# Revit family: Casement_34_G_Top_Hung_Standard
name_source: partatom
category: Windows
revit_build: Autodesk Revit 2014 (Build: 20130308_1515(x64)
units: mm (PartAtom-declared; Revit-internal decimal feet)

## types (12) — shared parameters
Aluminium Thickness = 1 mm  [stored 0.00328084 ft]
Bead SG Gap = 13 mm  [stored 0.0426509 ft]
Bottom Hung = No
Casement Dimension = 34 mm  [stored 0.111549 ft]
Custom Sash Height Bottom = 569 mm  [stored 1.8668 ft]
Custom Sash Height Top = 569 mm  [stored 1.8668 ft]
Custom Window Height = 1190 mm  [stored 3.9042 ft]
DG Extrusion Start = 7 mm  [stored 0.0229659 ft]
DG Gasket Finish = Double Glazing Gasket Material
DG Thickness Calc = 4 mm  [stored 0.0131234 ft]
Default Sill Height = 800 mm  [stored 2.62467 ft]
Depth Bead = 20 mm  [stored 0.0656168 ft]
Description = Window 34mm, Type G top hung
Frame Center Offset = 17 mm  [stored 0.0557743 ft]
Height = 1200 mm  [stored 3.93701 ft]
Height Panel 1 = 555 mm  [stored 1.82087 ft]
Height Panel 2 = 555 mm  [stored 1.82087 ft]
Height Panel 4 = 1140 mm  [stored 3.74016 ft]
Height Sash 1 = 539 mm
Height Sash 2 = 539 mm
Height Sash Bottom Opening = 569 mm  [stored 1.8668 ft]
Height Sash Top Opening = 569 mm  [stored 1.8668 ft]
Length Mullion = 1200 mm  [stored 3.93701 ft]
Limit Fixed Pane Height Max = 1800 mm
Limit Fixed Pane Height Min = 200 mm  [stored 0.656168 ft]
Limit Fixed Pane Width Max = 1500 mm
Limit Fixed Pane Width Min = 200 mm  [stored 0.656168 ft]
Limit Sash Bottom Height Max Based On Top Sash = 1229 mm
Limit Sash Height Bottom Max = 900 mm  [stored 2.95276 ft]
Limit Sash Height Bottom Min = 300 mm  [stored 0.984252 ft]
Limit Sash Height Top Max = 900 mm  [stored 2.95276 ft]
Limit Sash Height Top Min = 300 mm  [stored 0.984252 ft]
Limit Sash Width Max = 1200 mm  [stored 3.93701 ft]
Limit Sash Width Min = 300 mm  [stored 0.984252 ft]
Limit Window Height Max = 1860 mm
Manufacturer = Crealco
Max System DG One Piece Thickness = 4 mm  [stored 0.0131234 ft]
Max System DG Unit Thickness = 20 mm  [stored 0.0656168 ft]
Model = Casement 34
Offset Bead SG Center Reversed = 17 mm  [stored 0.0557743 ft]
Offset Sash 1 Top = 23 mm  [stored 0.0754593 ft]
Offset Sash 2 Top = 608 mm  [stored 1.99475 ft]
Offset Sash Left = 23 mm  [stored 0.0754593 ft]
Offset Transom 1 Top = 585 mm  [stored 1.91929 ft]
Offset Window Exterior = 17 mm  [stored 0.0557743 ft]
Rough Width = 16 mm  [stored 0.0524934 ft]
SG Gasket Thickness = 6 mm  [stored 0.019685 ft]
Sash Center Offset = 14 mm  [stored 0.0459318 ft]
Sash Overlap = 7 mm  [stored 0.0229659 ft]
Sash Spacing Inner = 8 mm  [stored 0.0262467 ft]
Top Hung = Yes
URL = http://www.crealco.co.za
Wall Closure = By host
Width Bead = 15 mm  [stored 0.0492126 ft]
Width Profile = 30 mm  [stored 0.0984252 ft]
zero-valued in all types: Window Exterior Offset

## per-type parameters (varying)
- 34-1212DT-1000Pa: Area Pane Left Bottom=0.25 m²; Area Pane Left Top=0.25 m²; Area Pane Right=0.6 m²; Clearvue Insulated LowE SHGC Value=0.658; Clearvue Insulated LowE U Value=4.66; Clearvue Insulated SHGC Value=0.723; Clearvue Insulated U Value=5.43; Clearvue SHGC Value=0.814; Clearvue U Value=8.2; Custom Sash Width=569 mm  [stored 1.8668 ft]; Custom Windload=1000 mm  [stored 3.28084 ft]; Custom Window Width=1190 mm  [stored 3.9042 ft]; Depth Mullion=35 mm; Energy Advantage SHGC Value=0.729; Energy Advantage U Value=6.26; Intruderprufe LowE SHGC Value=0.682; Intruderprufe LowE U Value=6.03; Intruderprufe SHGC Value=0.768; Intruderprufe U Value=8.08; Length Transom=555 mm  [stored 1.82087 ft]; Limit Window Width Max=2145 mm; Limit Window Width Min=845 mm  [stored 2.77231 ft]; Max Pane Area=0.6 m²; Mullion Depth Windload Based=35 mm; Offset Mullion Left=585 mm  [stored 1.91929 ft]; Offset Panel 4 Left=615 mm  [stored 2.01772 ft]; Width=1190 mm  [stored 3.9042 ft]; Width Panel 1=555 mm  [stored 1.82087 ft]; Width Panel 2=555 mm  [stored 1.82087 ft]; Width Panel 4=545 mm; Width Sash 1=539 mm; Width Sash 2=539 mm; Width Sash Opening=569 mm  [stored 1.8668 ft]; Windload Design=1000 mm  [stored 3.28084 ft]
- 34-1212DT-1500Pa: Area Pane Left Bottom=0.25 m²; Area Pane Left Top=0.25 m²; Area Pane Right=0.6 m²; Clearvue Insulated LowE SHGC Value=0.659; Clearvue Insulated LowE U Value=4.78; Clearvue Insulated SHGC Value=0.737; Clearvue Insulated U Value=5.35; Clearvue SHGC Value=0.814; Clearvue U Value=8.23; Custom Sash Width=569 mm  [stored 1.8668 ft]; Custom Windload=1500 mm; Custom Window Width=1190 mm  [stored 3.9042 ft]; Depth Mullion=54 mm  [stored 0.177165 ft]; Energy Advantage SHGC Value=0.73; Energy Advantage U Value=6.35; Intruderprufe LowE SHGC Value=0.684; Intruderprufe LowE U Value=6.12; Intruderprufe SHGC Value=0.766; Intruderprufe U Value=7.92; Length Transom=555 mm  [stored 1.82087 ft]; Limit Window Width Max=2145 mm; Limit Window Width Min=845 mm  [stored 2.77231 ft]; Max Pane Area=0.6 m²; Mullion Depth Windload Based=54 mm  [stored 0.177165 ft]; Offset Mullion Left=585 mm  [stored 1.91929 ft]; Offset Panel 4 Left=615 mm  [stored 2.01772 ft]; Width=1190 mm  [stored 3.9042 ft]; Width Panel 1=555 mm  [stored 1.82087 ft]; Width Panel 2=555 mm  [stored 1.82087 ft]; Width Panel 4=545 mm; Width Sash 1=539 mm; Width Sash 2=539 mm; Width Sash Opening=569 mm  [stored 1.8668 ft]; Windload Design=1500 mm
- 34-1212DT-2000Pa: Area Pane Left Bottom=0.25 m²; Area Pane Left Top=0.25 m²; Area Pane Right=0.6 m²; Clearvue Insulated LowE SHGC Value=0.659; Clearvue Insulated LowE U Value=4.78; Clearvue Insulated SHGC Value=0.737; Clearvue Insulated U Value=5.35; Clearvue SHGC Value=0.814; Clearvue U Value=8.23; Custom Sash Width=569 mm  [stored 1.8668 ft]; Custom Windload=2000 mm; Custom Window Width=1190 mm  [stored 3.9042 ft]; Depth Mullion=54 mm  [stored 0.177165 ft]; Energy Advantage SHGC Value=0.73; Energy Advantage U Value=6.35; Intruderprufe LowE SHGC Value=0.684; Intruderprufe LowE U Value=6.12; Intruderprufe SHGC Value=0.766; Intruderprufe U Value=7.92; Length Transom=555 mm  [stored 1.82087 ft]; Limit Window Width Max=2145 mm; Limit Window Width Min=845 mm  [stored 2.77231 ft]; Max Pane Area=0.6 m²; Mullion Depth Windload Based=54 mm  [stored 0.177165 ft]; Offset Mullion Left=585 mm  [stored 1.91929 ft]; Offset Panel 4 Left=615 mm  [stored 2.01772 ft]; Width=1190 mm  [stored 3.9042 ft]; Width Panel 1=555 mm  [stored 1.82087 ft]; Width Panel 2=555 mm  [stored 1.82087 ft]; Width Panel 4=545 mm; Width Sash 1=539 mm; Width Sash 2=539 mm; Width Sash Opening=569 mm  [stored 1.8668 ft]; Windload Design=2000 mm
- 34-1512DT-1000Pa: Area Pane Left Bottom=0.25 m²; Area Pane Left Top=0.25 m²; Area Pane Right=0.94 m²; Clearvue Insulated LowE SHGC Value=0.746; Clearvue Insulated LowE U Value=4.67; Clearvue Insulated SHGC Value=0.82; Clearvue Insulated U Value=5.53; Clearvue SHGC Value=0.924; Clearvue U Value=8.47; Custom Sash Width=569 mm  [stored 1.8668 ft]; Custom Windload=1000 mm  [stored 3.28084 ft]; Custom Window Width=1490 mm; Depth Mullion=35 mm; Energy Advantage SHGC Value=0.827; Energy Advantage U Value=6.5; Intruderprufe LowE SHGC Value=0.773; Intruderprufe LowE U Value=6.25; Intruderprufe SHGC Value=0.873; Intruderprufe U Value=8.6; Length Transom=555 mm  [stored 1.82087 ft]; Limit Window Width Max=2145 mm; Limit Window Width Min=845 mm  [stored 2.77231 ft]; Max Pane Area=0.94 m²; Mullion Depth Windload Based=35 mm; Offset Mullion Left=585 mm  [stored 1.91929 ft]; Offset Panel 4 Left=615 mm  [stored 2.01772 ft]; Width=1490 mm; Width Panel 1=555 mm  [stored 1.82087 ft]; Width Panel 2=555 mm  [stored 1.82087 ft]; Width Panel 4=845 mm  [stored 2.77231 ft]; Width Sash 1=539 mm; Width Sash 2=539 mm; Width Sash Opening=569 mm  [stored 1.8668 ft]; Windload Design=1000 mm  [stored 3.28084 ft]
- 34-1512DT-1500Pa: Area Pane Left Bottom=0.25 m²; Area Pane Left Top=0.25 m²; Area Pane Right=0.94 m²; Clearvue Insulated LowE SHGC Value=0.747; Clearvue Insulated LowE U Value=4.77; Clearvue Insulated SHGC Value=0.832; Clearvue Insulated U Value=5.47; Clearvue SHGC Value=0.924; Clearvue U Value=8.81; Custom Sash Width=569 mm  [stored 1.8668 ft]; Custom Windload=1500 mm; Custom Window Width=1490 mm; Depth Mullion=54 mm  [stored 0.177165 ft]; Energy Advantage SHGC Value=0.828; Energy Advantage U Value=6.58; Intruderprufe LowE SHGC Value=0.775; Intruderprufe LowE U Value=6.33; Intruderprufe SHGC Value=0.871; Intruderprufe U Value=8.46; Length Transom=555 mm  [stored 1.82087 ft]; Limit Window Width Max=2145 mm; Limit Window Width Min=845 mm  [stored 2.77231 ft]; Max Pane Area=0.94 m²; Mullion Depth Windload Based=54 mm  [stored 0.177165 ft]; Offset Mullion Left=585 mm  [stored 1.91929 ft]; Offset Panel 4 Left=615 mm  [stored 2.01772 ft]; Width=1490 mm; Width Panel 1=555 mm  [stored 1.82087 ft]; Width Panel 2=555 mm  [stored 1.82087 ft]; Width Panel 4=845 mm  [stored 2.77231 ft]; Width Sash 1=539 mm; Width Sash 2=539 mm; Width Sash Opening=569 mm  [stored 1.8668 ft]; Windload Design=1500 mm
- 34-1512DT-2000Pa: Area Pane Left Bottom=0.25 m²; Area Pane Left Top=0.25 m²; Area Pane Right=0.94 m²; Clearvue Insulated LowE SHGC Value=0.747; Clearvue Insulated LowE U Value=4.77; Clearvue Insulated SHGC Value=0.832; Clearvue Insulated U Value=5.47; Clearvue SHGC Value=0.924; Clearvue U Value=8.81; Custom Sash Width=569 mm  [stored 1.8668 ft]; Custom Windload=2000 mm; Custom Window Width=1490 mm; Depth Mullion=54 mm  [stored 0.177165 ft]; Energy Advantage SHGC Value=0.828; Energy Advantage U Value=6.58; Intruderprufe LowE SHGC Value=0.775; Intruderprufe LowE U Value=6.33; Intruderprufe SHGC Value=0.871; Intruderprufe U Value=8.46; Length Transom=555 mm  [stored 1.82087 ft]; Limit Window Width Max=2145 mm; Limit Window Width Min=845 mm  [stored 2.77231 ft]; Max Pane Area=0.94 m²; Mullion Depth Windload Based=54 mm  [stored 0.177165 ft]; Offset Mullion Left=585 mm  [stored 1.91929 ft]; Offset Panel 4 Left=615 mm  [stored 2.01772 ft]; Width=1490 mm; Width Panel 1=555 mm  [stored 1.82087 ft]; Width Panel 2=555 mm  [stored 1.82087 ft]; Width Panel 4=845 mm  [stored 2.77231 ft]; Width Sash 1=539 mm; Width Sash 2=539 mm; Width Sash Opening=569 mm  [stored 1.8668 ft]; Windload Design=2000 mm
- 34-1812DT-1000Pa: Area Pane Left Bottom=0.41 m²; Area Pane Left Top=0.41 m²; Area Pane Right=0.91 m²; Clearvue Insulated LowE SHGC Value=0.701; Clearvue Insulated LowE U Value=4.3; Clearvue Insulated SHGC Value=0.771; Clearvue Insulated U Value=5.11; Clearvue SHGC Value=0.869; Clearvue U Value=8.14; Custom Sash Width=900 mm  [stored 2.95276 ft]; Custom Windload=1000 mm  [stored 3.28084 ft]; Custom Window Width=1790 mm; Depth Mullion=35 mm; Energy Advantage SHGC Value=0.778; Energy Advantage U Value=6.03; Intruderprufe LowE SHGC Value=0.727; Intruderprufe LowE U Value=5.81; Intruderprufe SHGC Value=0.821; Intruderprufe U Value=7.99; Length Transom=886 mm  [stored 2.90682 ft]; Limit Window Width Max=2476 mm; Limit Window Width Min=1176 mm  [stored 3.85827 ft]; Max Pane Area=0.91 m²; Mullion Depth Windload Based=35 mm; Offset Mullion Left=916 mm  [stored 3.00525 ft]; Offset Panel 4 Left=946 mm; Width=1790 mm; Width Panel 1=886 mm  [stored 2.90682 ft]; Width Panel 2=886 mm  [stored 2.90682 ft]; Width Panel 4=814 mm; Width Sash 1=870 mm  [stored 2.85433 ft]; Width Sash 2=870 mm  [stored 2.85433 ft]; Width Sash Opening=900 mm  [stored 2.95276 ft]; Windload Design=1000 mm  [stored 3.28084 ft]
- 34-1812DT-1500Pa: Area Pane Left Bottom=0.41 m²; Area Pane Left Top=0.41 m²; Area Pane Right=0.91 m²; Clearvue Insulated LowE SHGC Value=0.702; Clearvue Insulated LowE U Value=4.39; Clearvue Insulated SHGC Value=0.78; Clearvue Insulated U Value=5.06; Clearvue SHGC Value=0.869; Clearvue U Value=8.19; Custom Sash Width=900 mm  [stored 2.95276 ft]; Custom Windload=1500 mm; Custom Window Width=1790 mm; Depth Mullion=54 mm  [stored 0.177165 ft]; Energy Advantage SHGC Value=0.778; Energy Advantage U Value=6.09; Intruderprufe LowE SHGC Value=0.728; Intruderprufe LowE U Value=5.87; Intruderprufe SHGC Value=0.82; Intruderprufe U Value=7.88; Length Transom=886 mm  [stored 2.90682 ft]; Limit Window Width Max=2476 mm; Limit Window Width Min=1176 mm  [stored 3.85827 ft]; Max Pane Area=0.91 m²; Mullion Depth Windload Based=54 mm  [stored 0.177165 ft]; Offset Mullion Left=916 mm  [stored 3.00525 ft]; Offset Panel 4 Left=946 mm; Width=1790 mm; Width Panel 1=886 mm  [stored 2.90682 ft]; Width Panel 2=886 mm  [stored 2.90682 ft]; Width Panel 4=814 mm; Width Sash 1=870 mm  [stored 2.85433 ft]; Width Sash 2=870 mm  [stored 2.85433 ft]; Width Sash Opening=900 mm  [stored 2.95276 ft]; Windload Design=1500 mm
- 34-1812DT-2000Pa: Area Pane Left Bottom=0.41 m²; Area Pane Left Top=0.41 m²; Area Pane Right=0.91 m²; Clearvue Insulated LowE SHGC Value=0.702; Clearvue Insulated LowE U Value=4.39; Clearvue Insulated SHGC Value=0.78; Clearvue Insulated U Value=5.06; Clearvue SHGC Value=0.869; Clearvue U Value=8.19; Custom Sash Width=900 mm  [stored 2.95276 ft]; Custom Windload=2000 mm; Custom Window Width=1790 mm; Depth Mullion=54 mm  [stored 0.177165 ft]; Energy Advantage SHGC Value=0.778; Energy Advantage U Value=6.09; Intruderprufe LowE SHGC Value=0.728; Intruderprufe LowE U Value=5.87; Intruderprufe SHGC Value=0.82; Intruderprufe U Value=7.88; Length Transom=886 mm  [stored 2.90682 ft]; Limit Window Width Max=2476 mm; Limit Window Width Min=1176 mm  [stored 3.85827 ft]; Max Pane Area=0.91 m²; Mullion Depth Windload Based=54 mm  [stored 0.177165 ft]; Offset Mullion Left=916 mm  [stored 3.00525 ft]; Offset Panel 4 Left=946 mm; Width=1790 mm; Width Panel 1=886 mm  [stored 2.90682 ft]; Width Panel 2=886 mm  [stored 2.90682 ft]; Width Panel 4=814 mm; Width Sash 1=870 mm  [stored 2.85433 ft]; Width Sash 2=870 mm  [stored 2.85433 ft]; Width Sash Opening=900 mm  [stored 2.95276 ft]; Windload Design=2000 mm
- 34-2412DT-1000Pa: Area Pane Left Bottom=0.41 m²; Area Pane Left Top=0.41 m²; Area Pane Right=1.59 m²; Clearvue Insulated LowE SHGC Value=0.553; Clearvue Insulated LowE U Value=3.04; Clearvue Insulated SHGC Value=0.615; Clearvue Insulated U Value=3.58; Clearvue SHGC Value=0; Clearvue U Value=7.9; Custom Sash Width=900 mm  [stored 2.95276 ft]; Custom Windload=1000 mm  [stored 3.28084 ft]; Custom Window Width=2390 mm; Depth Mullion=54 mm  [stored 0.177165 ft]; Energy Advantage SHGC Value=0; Energy Advantage U Value=7.9; Intruderprufe LowE SHGC Value=0.574; Intruderprufe LowE U Value=4.22; Intruderprufe SHGC Value=0.648; Intruderprufe U Value=5.85; Length Transom=886 mm  [stored 2.90682 ft]; Limit Window Width Max=2476 mm; Limit Window Width Min=1176 mm  [stored 3.85827 ft]; Max Pane Area=1.59 m²; Mullion Depth Windload Based=54 mm  [stored 0.177165 ft]; Offset Mullion Left=916 mm  [stored 3.00525 ft]; Offset Panel 4 Left=946 mm; Width=2390 mm; Width Panel 1=886 mm  [stored 2.90682 ft]; Width Panel 2=886 mm  [stored 2.90682 ft]; Width Panel 4=1414 mm; Width Sash 1=870 mm  [stored 2.85433 ft]; Width Sash 2=870 mm  [stored 2.85433 ft]; Width Sash Opening=900 mm  [stored 2.95276 ft]; Windload Design=1000 mm  [stored 3.28084 ft]
- 34-2412DT-1500Pa: Area Pane Left Bottom=0.41 m²; Area Pane Left Top=0.41 m²; Area Pane Right=1.59 m²; Clearvue Insulated LowE SHGC Value=0.553; Clearvue Insulated LowE U Value=3.04; Clearvue Insulated SHGC Value=0.615; Clearvue Insulated U Value=3.58; Clearvue SHGC Value=0; Clearvue U Value=7.9; Custom Sash Width=900 mm  [stored 2.95276 ft]; Custom Windload=1500 mm; Custom Window Width=2390 mm; Depth Mullion=54 mm  [stored 0.177165 ft]; Energy Advantage SHGC Value=0; Energy Advantage U Value=7.9; Intruderprufe LowE SHGC Value=0.574; Intruderprufe LowE U Value=4.22; Intruderprufe SHGC Value=0.648; Intruderprufe U Value=5.85; Length Transom=886 mm  [stored 2.90682 ft]; Limit Window Width Max=2476 mm; Limit Window Width Min=1176 mm  [stored 3.85827 ft]; Max Pane Area=1.59 m²; Mullion Depth Windload Based=54 mm  [stored 0.177165 ft]; Offset Mullion Left=916 mm  [stored 3.00525 ft]; Offset Panel 4 Left=946 mm; Width=2390 mm; Width Panel 1=886 mm  [stored 2.90682 ft]; Width Panel 2=886 mm  [stored 2.90682 ft]; Width Panel 4=1414 mm; Width Sash 1=870 mm  [stored 2.85433 ft]; Width Sash 2=870 mm  [stored 2.85433 ft]; Width Sash Opening=900 mm  [stored 2.95276 ft]; Windload Design=1500 mm
- 34-2412DT-2000Pa: Area Pane Left Bottom=0.41 m²; Area Pane Left Top=0.41 m²; Area Pane Right=1.59 m²; Clearvue Insulated LowE SHGC Value=0.553; Clearvue Insulated LowE U Value=3.04; Clearvue Insulated SHGC Value=0.615; Clearvue Insulated U Value=3.58; Clearvue SHGC Value=0; Clearvue U Value=7.9; Custom Sash Width=900 mm  [stored 2.95276 ft]; Custom Windload=2000 mm; Custom Window Width=2390 mm; Depth Mullion=54 mm  [stored 0.177165 ft]; Energy Advantage SHGC Value=0; Energy Advantage U Value=7.9; Intruderprufe LowE SHGC Value=0.574; Intruderprufe LowE U Value=4.22; Intruderprufe SHGC Value=0.648; Intruderprufe U Value=5.85; Length Transom=886 mm  [stored 2.90682 ft]; Limit Window Width Max=2476 mm; Limit Window Width Min=1176 mm  [stored 3.85827 ft]; Max Pane Area=1.59 m²; Mullion Depth Windload Based=54 mm  [stored 0.177165 ft]; Offset Mullion Left=916 mm  [stored 3.00525 ft]; Offset Panel 4 Left=946 mm; Width=2390 mm; Width Panel 1=886 mm  [stored 2.90682 ft]; Width Panel 2=886 mm  [stored 2.90682 ft]; Width Panel 4=1414 mm; Width Sash 1=870 mm  [stored 2.85433 ft]; Width Sash 2=870 mm  [stored 2.85433 ft]; Width Sash Opening=900 mm  [stored 2.95276 ft]; Windload Design=2000 mm

note: [stored X ft] marks values corroborated as IEEE doubles in the binary element streams (Revit-internal decimal feet)

## geometry (parser evidence)
native form markers: Blend x4, Extrusion x1, Sweep x28
no freeform markers — native parametric forms only
